# Revit family: Fam Bticino portier système IP standard poste intérieur
name_source: partatom
category: Tableaux/Baies
units: mm (PartAtom-declared; Revit-internal decimal feet)

## family parameters
Configuration du panneau = Deux colonnes, circuits au sein
Conserver l'orientation des annotations = Non
Cote de connecteur circulaire = Utiliser le diamètre
Couper avec des vides une fois chargée = Non
Hôte = Face
Partagée = Non
Repère de localisation dans la pièce = Non
Type d'élément = Tableau de raccordement

## types (4) — shared parameters
Avec caméra = Non
Classe Etim = LC000779 téléphone pour villa
Conditions générales d'utilisation = https://assets.legrand.com
Ecran tactile = Oui
Elévation par défaut = 1500 mm  [stored 4.92126 ft]
Fabricant = BTICINO
Hauteur = 122 mm  [stored 0.400262 ft]
IP = 30
Largeur = 189 mm  [stored 0.620079 ft]
Mode de pose = Saillie
Photo = https://assets.legrand.com
Temperature utilisation min max = -10/+40 °C
Type de raccordement = Câble RJ45
Type interface = Réseau filaire

## per-type parameters (varying)
| type | Contour champagne | Contour miroir | Couleur | Désignation produit | EAN | Plaque champagne | Plaque miroir | Plaque noire | Référence | Tension |
| Type standard noir 24V | Non | Oui | Noir | Bticino portier IP standard poste intérieur noir BT-373005 | 8005543710722 | Non | Non | Oui | BT-373005 | 24 V DC |
| Type standard champagne | Oui | Non | Champagne | Bticino portier IP standard poste intérieur champagne BT-373006 | 8005543710746 | Oui | Non | Non | BT-373006 | 24 V DC |
| Type standard miroir | Oui | Non | Miroir | Bticino portier IP standard poste intérieur miroir BT-373007 | 8005543710760 | Non | Oui | Non | BT-373007 | 24 V DC |
| Type standard noir 48V | Non | Oui | Noir | BTicino portier IP standard poste intérieur noir BT-373008 | 8005543744451 | Non | Non | Oui | BT-373008 | 48 V DC |

note: [stored X ft] marks values corroborated as IEEE doubles in the binary element streams (Revit-internal decimal feet)
